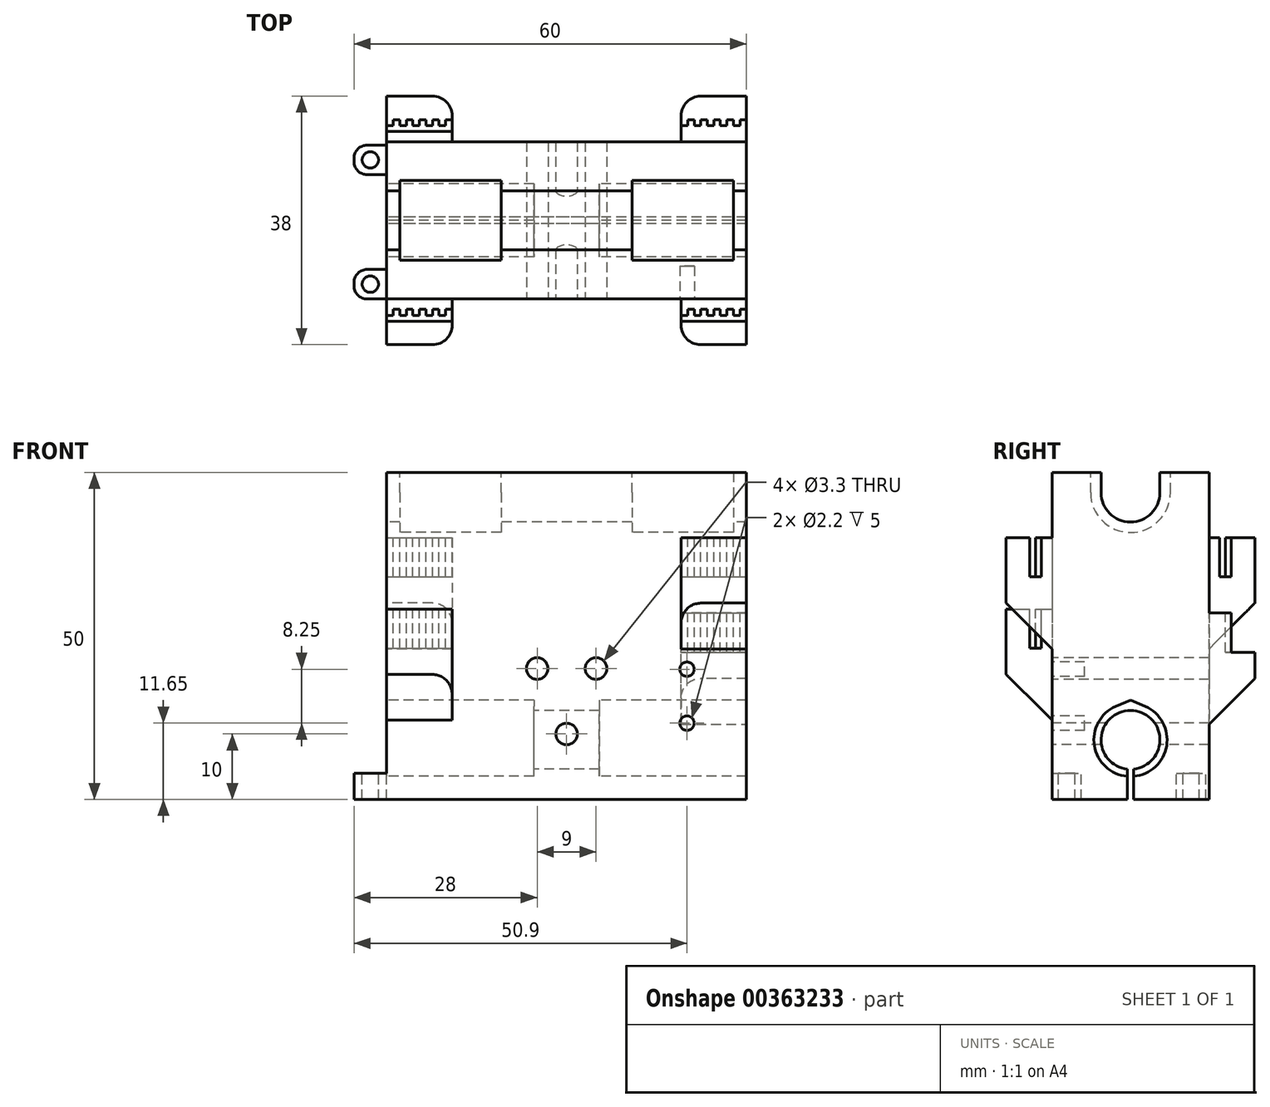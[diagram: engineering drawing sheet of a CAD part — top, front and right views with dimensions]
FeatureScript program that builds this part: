
annotation { "Feature Type Name" : "Feature", "Feature Type Description" : "" }
export const myFeature = defineFeature(function(context is Context, id is Id, definition is map)
    precondition{}
    {
        {
            var Q0;
            Q0=qCreatedBy(makeId("Top.planeOp"),FACE);
            var sketch = newSketch(context, id + "F0", { "sketchPlane" : qUnion([Q0])});
            skLineSegment(sketch, "E0.bottom", {"start": v(0, 0) * mm, "end": v(55, 0) * mm});
            skLineSegment(sketch, "E0.top", {"start": v(0, 24) * mm, "end": v(55, 24) * mm});
            skLineSegment(sketch, "E0.left", {"start": v(0, 0) * mm, "end": v(0, 24) * mm});
            skLineSegment(sketch, "E0.right", {"start": v(55, 0) * mm, "end": v(55, 24) * mm});
            skSolve(sketch);
        }
        {
            var Q0;
            Q0=qSketchRegion(id+"F0",true);
            extrude(context, id + "F1", {"entities" : qUnion([Q0]), "depth" : 50 * mm});
        }
        {
            var Q0;
            Q0=makeQuery(id+"F1.opExtrude","SWEPT_FACE",FACE,{"disambiguationData":[OSD([sQuery(id+"F0.wireOp",EDGE,"E0.left")])]});
            var sketch = newSketch(context, id + "F2", { "sketchPlane" : qUnion([Q0])});
            skCircle(sketch, "E1", {"center": v(-12, 9.1) * mm, "radius": 5.6 * mm});
            skCircle(sketch, "E2", {"center": v(-12, 46.9) * mm, "radius": 4.5 * mm});
            skLineSegment(sketch, "E3", {"start": v(-24, 46.9) * mm, "end": v(0, 46.9) * mm, "construction": true});
            skLineSegment(sketch, "E4", {"start": v(-16.5, 50) * mm, "end": v(-16.5, 46.9) * mm});
            skLineSegment(sketch, "E5", {"start": v(-7.5, 50) * mm, "end": v(-7.5, 46.9) * mm});
            skLineSegment(sketch, "E6", {"start": v(-24, 9.1) * mm, "end": v(0, 9.1) * mm, "construction": true});
            skLineSegment(sketch, "E7", {"start": v(-12, 9.1) * mm, "end": v(-12, 0) * mm, "construction": true});
            skLineSegment(sketch, "E8", {"start": v(-12, 0) * mm, "end": v(-12.5, 0) * mm});
            skLineSegment(sketch, "E9", {"start": v(-12.5, 0) * mm, "end": v(-12.5, 4.63) * mm});
            skLineSegment(sketch, "E10", {"start": v(-12.5, 4.63) * mm, "end": v(-11.5, 4.63) * mm});
            skLineSegment(sketch, "E11", {"start": v(-11.5, 4.63) * mm, "end": v(-11.5, 0) * mm});
            skLineSegment(sketch, "E12", {"start": v(-11.5, 0) * mm, "end": v(-12, 0) * mm});
            skCircle(sketch, "E13", {"center": v(-12, 46.9) * mm, "radius": 6.1 * mm});
            skLineSegment(sketch, "E14", {"start": v(-5.9, 46.9) * mm, "end": v(-5.9, 50) * mm});
            skLineSegment(sketch, "E15", {"start": v(-18.1, 46.9) * mm, "end": v(-18.1, 50) * mm});
            skLineSegment(sketch, "E16", {"start": v(-12, 9.1) * mm, "end": v(-12, 14.7) * mm, "construction": true});
            skLineSegment(sketch, "E17", {"start": v(-12, 14.7) * mm, "end": v(-12, 15.2) * mm, "construction": true});
            skLineSegment(sketch, "E18", {"start": v(-9.73, 14.22) * mm, "end": v(-14.27, 14.22) * mm, "construction": true});
            skLineSegment(sketch, "E19", {"start": v(-12, 15.2) * mm, "end": v(-9.73, 14.22) * mm});
            skLineSegment(sketch, "E20", {"start": v(-12, 15.2) * mm, "end": v(-14.27, 14.22) * mm});
            skCircle(sketch, "E21", {"center": v(-12, 9.1) * mm, "radius": 4.5 * mm});
            skSolve(sketch);
        }
        {
            var Q0;
            {var subQ0=sQuery(id+"F2.wireOp",EDGE,"61a55092-bd36-442a-954f-b1d305e603b2");var subQ1=sQuery(id+"F2.wireOp",EDGE,"E1");var subQ3=makeQuery(id+"F2.imprint","INTERSECT",VERTEX,{"disambiguationData":[OD(0.0)],"derivedFrom":[subQ1,subQ0]});Q0=makeQuery(id+"F2.imprint","IMPRINT",FACE,{"disambiguationData":[TD([[makeQuery(id+"F2.imprint","IMPRINT",EDGE,{"disambiguationData":[TD([[subQ3,-1.0]])],"derivedFrom":subQ1}),1.0]])]});}
            var Q1;
            {var subQ0=sQuery(id+"F2.wireOp",EDGE,"ccdeb851-c584-4ba8-b480-4501c20c5f95");var subQ1=sQuery(id+"F2.wireOp",EDGE,"E1");var subQ3=makeQuery(id+"F2.imprint","INTERSECT",VERTEX,{"disambiguationData":[OD(0.0)],"derivedFrom":[subQ1,subQ0]});Q1=makeQuery(id+"F2.imprint","IMPRINT",FACE,{"disambiguationData":[TD([[makeQuery(id+"F2.imprint","IMPRINT",EDGE,{"disambiguationData":[TD([[subQ3,1.0]])],"derivedFrom":subQ1}),1.0]])]});}
            var Q2;
            Q2=makeQuery(id+"F2.imprint","IMPRINT",FACE,{"disambiguationData":[TD([[makeQuery(id+"F2.imprint","IMPRINT",EDGE,{"derivedFrom":sQuery(id+"F2.wireOp",EDGE,"E8")}),-1.0]])]});
            var Q3;
            {var subQ0=sQuery(id+"F2.wireOp",EDGE,"E10");Q3=makeQuery(id+"F2.imprint","IMPRINT",FACE,{"disambiguationData":[TD([[makeQuery(id+"F2.imprint","IMPRINT",EDGE,{"derivedFrom":subQ0}),-1.0]])]});}
            var Q4;
            {var subQ3=sQuery(id+"F2.wireOp",EDGE,"84843404-b723-4df1-a710-1511c094684b");Q4=makeQuery(id+"F2.imprint","IMPRINT",FACE,{"disambiguationData":[TD([[makeQuery(id+"F2.imprint","IMPRINT",EDGE,{"derivedFrom":subQ3}),-1.0]])]});}
            var Q5;
            {var subQ3=sQuery(id+"F2.wireOp",EDGE,"84843404-b723-4df1-a710-1511c094684b");Q5=makeQuery(id+"F2.imprint","IMPRINT",FACE,{"disambiguationData":[TD([[makeQuery(id+"F2.imprint","IMPRINT",EDGE,{"derivedFrom":subQ3}),1.0]])]});}
            var Q6;
            {var subQ3=sQuery(id+"F2.wireOp",EDGE,"E5");Q6=makeQuery(id+"F2.imprint","IMPRINT",FACE,{"disambiguationData":[TD([[makeQuery(id+"F2.imprint","IMPRINT",EDGE,{"derivedFrom":subQ3}),-1.0]])]});}
            var Q7;
            {var subQ0=sQuery(id+"F2.wireOp",EDGE,"E4");Q7=makeQuery(id+"F2.imprint","IMPRINT",FACE,{"disambiguationData":[TD([[makeQuery(id+"F2.imprint","IMPRINT",EDGE,{"derivedFrom":subQ0}),1.0]])]});}
            var Q8;
            {var subQ0=sQuery(id+"F2.wireOp",EDGE,"E4");Q8=makeQuery(id+"F2.imprint","IMPRINT",FACE,{"disambiguationData":[TD([[makeQuery(id+"F2.imprint","IMPRINT",EDGE,{"derivedFrom":subQ0}),1.0]])]});}
            var Q9;
            {var subQ3=sQuery(id+"F2.wireOp",EDGE,"E5");Q9=makeQuery(id+"F2.imprint","IMPRINT",FACE,{"disambiguationData":[TD([[makeQuery(id+"F2.imprint","IMPRINT",EDGE,{"derivedFrom":subQ3}),-1.0]])]});}
            var Q10;
            {var subQ1=sQuery(id+"F2.wireOp",EDGE,"E2");var subQ4=makeQuery(id+"F2.imprint","INTERSECT",VERTEX,{"derivedFrom":[subQ1,sQuery(id+"F2.wireOp",EDGE,"E5")]});Q10=makeQuery(id+"F2.imprint","IMPRINT",FACE,{"disambiguationData":[TD([[makeQuery(id+"F2.imprint","IMPRINT",EDGE,{"disambiguationData":[TD([[subQ4,-1.0]])],"derivedFrom":subQ1}),1.0]])]});}
            var Q11;
            Q11=makeQuery(id+"F2.imprint","IMPRINT",FACE,{"disambiguationData":[TD([[makeQuery(id+"F2.imprint","IMPRINT",EDGE,{"derivedFrom":sQuery(id+"F2.wireOp",EDGE,"E21")}),1.0]])]});
            var Q12;
            Q12=makeQuery(id+"F1.opExtrude","SWEPT_FACE",FACE,{"disambiguationData":[OSD([sQuery(id+"F0.wireOp",EDGE,"E0.right")])]});
            var Q13;
            {var subQ0=sQuery(id+"F2.wireOp",EDGE,"E9");var subQ1=sQuery(id+"F2.wireOp",EDGE,"E1");var subQ2=makeQuery(id+"F2.imprint","INTERSECT",VERTEX,{"derivedFrom":[subQ1,subQ0]});Q13=makeQuery(id+"F2.imprint","IMPRINT",FACE,{"disambiguationData":[TD([[makeQuery(id+"F2.imprint","IMPRINT",EDGE,{"disambiguationData":[TD([[subQ2,-1.0]])],"derivedFrom":subQ1}),1.0]])]});}
            extrude(context, id + "F3", {"entities" : qUnion([Q0, Q1, Q2, Q3, Q4, Q5, Q6, Q7, Q8, Q9, Q10, Q11, Q12, Q13]), "operationType" : NewBodyOperationType.REMOVE, "endBound" : BoundingType.THROUGH_ALL, "oppositeDirection" : true, "depth" : 25 * mm});
        }
        {
            var Q0;
            {var subQ3=sQuery(id+"F2.wireOp",EDGE,"E4");Q0=makeQuery(id+"F2.imprint","IMPRINT",FACE,{"disambiguationData":[TD([[makeQuery(id+"F2.imprint","IMPRINT",EDGE,{"derivedFrom":subQ3}),-1.0]])]});}
            var Q1;
            {var subQ3=sQuery(id+"F2.wireOp",EDGE,"E15");Q1=makeQuery(id+"F2.imprint","IMPRINT",FACE,{"disambiguationData":[TD([[makeQuery(id+"F2.imprint","IMPRINT",EDGE,{"derivedFrom":subQ3}),-1.0]])]});}
            var Q2;
            {var subQ3=sQuery(id+"F2.wireOp",EDGE,"E14");Q2=makeQuery(id+"F2.imprint","IMPRINT",FACE,{"disambiguationData":[TD([[makeQuery(id+"F2.imprint","IMPRINT",EDGE,{"derivedFrom":subQ3}),1.0]])]});}
            extrude(context, id + "F4", {"entities" : qUnion([Q0, Q1, Q2]), "operationType" : NewBodyOperationType.REMOVE, "oppositeDirection" : true, "depth" : 53 * mm});
        }
        {
            var Q0;
            {var subQ3=sQuery(id+"F2.wireOp",EDGE,"E4");Q0=makeQuery(id+"F2.imprint","IMPRINT",FACE,{"disambiguationData":[TD([[makeQuery(id+"F2.imprint","IMPRINT",EDGE,{"derivedFrom":subQ3}),-1.0]])]});}
            var Q1;
            {var subQ3=sQuery(id+"F2.wireOp",EDGE,"E15");Q1=makeQuery(id+"F2.imprint","IMPRINT",FACE,{"disambiguationData":[TD([[makeQuery(id+"F2.imprint","IMPRINT",EDGE,{"derivedFrom":subQ3}),-1.0]])]});}
            var Q2;
            {var subQ3=sQuery(id+"F2.wireOp",EDGE,"E14");Q2=makeQuery(id+"F2.imprint","IMPRINT",FACE,{"disambiguationData":[TD([[makeQuery(id+"F2.imprint","IMPRINT",EDGE,{"derivedFrom":subQ3}),1.0]])]});}
            extrude(context, id + "F5", {"entities" : qUnion([Q0, Q1, Q2]), "operationType" : NewBodyOperationType.ADD, "oppositeDirection" : true, "depth" : 2 * mm});
        }
        {
            var Q0;
            Q0=makeQuery(id+"F5.opExtrude","CAP_FACE",FACE,{"disambiguationData":[OSD([sQuery(id+"F0.wireOp",EDGE,"E0.left"),sQuery(id+"F2.wireOp",EDGE,"E2"),sQuery(id+"F2.wireOp",EDGE,"E4"),sQuery(id+"F2.wireOp",EDGE,"E5"),sQuery(id+"F2.wireOp",EDGE,"E13"),sQuery(id+"F2.wireOp",EDGE,"E14"),sQuery(id+"F2.wireOp",EDGE,"E15")])],"isStart":false});
            extrude(context, id + "F6", {"entities" : qUnion([Q0]), "operationType" : NewBodyOperationType.ADD, "depth" : 35.5 * mm, "hasSecondDirection" : true, "secondDirectionOppositeDirection" : false, "secondDirectionDepth" : 15.5 * mm});
        }
        {
            var Q0;
            {var subQ0=sQuery(id+"F2.wireOp",EDGE,"E10");Q0=makeQuery(id+"F2.imprint","IMPRINT",FACE,{"disambiguationData":[TD([[makeQuery(id+"F2.imprint","IMPRINT",EDGE,{"derivedFrom":subQ0}),1.0]])]});}
            var Q1;
            {var subQ4=sQuery(id+"F2.wireOp",EDGE,"E1");var subQ8=sQuery(id+"F2.wireOp",EDGE,"E19");var subQ13=makeQuery(id+"F2.imprint","INTERSECT",VERTEX,{"disambiguationData":[OD(1.0)],"derivedFrom":[subQ4,subQ8]});Q1=makeQuery(id+"F2.imprint","IMPRINT",FACE,{"disambiguationData":[TD([[makeQuery(id+"F2.imprint","IMPRINT",EDGE,{"disambiguationData":[TD([[subQ13,-1.0]])],"derivedFrom":subQ4}),1.0]])]});}
            var Q2;
            {var subQ0=sQuery(id+"F2.wireOp",EDGE,"E19");var subQ1=sQuery(id+"F2.wireOp",EDGE,"E1");var subQ2=makeQuery(id+"F2.imprint","INTERSECT",VERTEX,{"disambiguationData":[OD(1.0)],"derivedFrom":[subQ1,subQ0]});Q2=makeQuery(id+"F2.imprint","IMPRINT",FACE,{"disambiguationData":[TD([[makeQuery(id+"F2.imprint","IMPRINT",EDGE,{"disambiguationData":[TD([[subQ2,-1.0]])],"derivedFrom":subQ1}),-1.0]])]});}
            extrude(context, id + "F7", {"entities" : qUnion([Q0, Q1, Q2]), "operationType" : NewBodyOperationType.REMOVE, "oppositeDirection" : true, "depth" : 22.5 * mm});
        }
        {
            var Q0;
            {var subQ0=sQuery(id+"F2.wireOp",EDGE,"E10");Q0=makeQuery(id+"F2.imprint","IMPRINT",FACE,{"disambiguationData":[TD([[makeQuery(id+"F2.imprint","IMPRINT",EDGE,{"derivedFrom":subQ0}),1.0]])]});}
            var Q1;
            {var subQ4=sQuery(id+"F2.wireOp",EDGE,"E1");var subQ8=sQuery(id+"F2.wireOp",EDGE,"E19");var subQ13=makeQuery(id+"F2.imprint","INTERSECT",VERTEX,{"disambiguationData":[OD(1.0)],"derivedFrom":[subQ4,subQ8]});Q1=makeQuery(id+"F2.imprint","IMPRINT",FACE,{"disambiguationData":[TD([[makeQuery(id+"F2.imprint","IMPRINT",EDGE,{"disambiguationData":[TD([[subQ13,-1.0]])],"derivedFrom":subQ4}),1.0]])]});}
            var Q2;
            {var subQ0=sQuery(id+"F2.wireOp",EDGE,"E19");var subQ1=sQuery(id+"F2.wireOp",EDGE,"E1");var subQ2=makeQuery(id+"F2.imprint","INTERSECT",VERTEX,{"disambiguationData":[OD(1.0)],"derivedFrom":[subQ1,subQ0]});Q2=makeQuery(id+"F2.imprint","IMPRINT",FACE,{"disambiguationData":[TD([[makeQuery(id+"F2.imprint","IMPRINT",EDGE,{"disambiguationData":[TD([[subQ2,-1.0]])],"derivedFrom":subQ1}),-1.0]])]});}
            var Q3;
            Q3=makeQuery(id+"F1.opExtrude","SWEPT_FACE",FACE,{"disambiguationData":[OSD([sQuery(id+"F0.wireOp",EDGE,"E0.right")])]});
            extrude(context, id + "F8", {"entities" : qUnion([Q0, Q1, Q2]), "operationType" : NewBodyOperationType.REMOVE, "endBound" : BoundingType.UP_TO_SURFACE, "oppositeDirection" : true, "endBoundEntityFace" : qUnion([Q3]), "depth" : 25 * mm, "hasSecondDirection" : true, "secondDirectionOppositeDirection" : true, "secondDirectionDepth" : 32.5 * mm});
        }
        {
            var Q0;
            Q0=makeQuery(id+"F1.opExtrude","SWEPT_FACE",FACE,{"disambiguationData":[OSD([sQuery(id+"F0.wireOp",EDGE,"E0.bottom")])]});
            var sketch = newSketch(context, id + "F9", { "sketchPlane" : qUnion([Q0])});
            skLineSegment(sketch, "E22.bottom", {"start": v(0, 29.1) * mm, "end": v(10, 29.1) * mm});
            skLineSegment(sketch, "E22.top", {"start": v(0, 9.1) * mm, "end": v(10, 9.1) * mm});
            skLineSegment(sketch, "E22.left", {"start": v(0, 29.1) * mm, "end": v(0, 9.1) * mm});
            skLineSegment(sketch, "E22.right", {"start": v(10, 29.1) * mm, "end": v(10, 9.1) * mm});
            skLineSegment(sketch, "E23.bottom", {"start": v(55, 40) * mm, "end": v(45, 40) * mm});
            skLineSegment(sketch, "E23.top", {"start": v(55, 20) * mm, "end": v(45, 20) * mm});
            skLineSegment(sketch, "E23.left", {"start": v(55, 40) * mm, "end": v(55, 20) * mm});
            skLineSegment(sketch, "E23.right", {"start": v(45, 40) * mm, "end": v(45, 20) * mm});
            skPoint(sketch, "E24", {"position": v(0, 47) * mm});
            skPoint(sketch, "E25", {"position": v(0, 8.6) * mm});
            skSolve(sketch);
        }
        {
            var Q0;
            Q0=qSketchRegion(id+"F9",true);
            extrude(context, id + "F10", {"entities" : qUnion([Q0]), "operationType" : NewBodyOperationType.ADD, "depth" : 7 * mm});
        }
        {
            var Q0;
            Q0=makeQuery(id+"F10.opExtrude","CAP_EDGE",EDGE,{"disambiguationData":[OSD([sQuery(id+"F9.wireOp",EDGE,"E22.top")])],"isStart":false});
            var Q1;
            Q1=makeQuery(id+"F10.opExtrude","CAP_EDGE",EDGE,{"disambiguationData":[OSD([sQuery(id+"F9.wireOp",EDGE,"E23.top")])],"isStart":false});
            chamfer(context, id + "F11", {"entities" : qUnion([Q0, Q1]), "width" : 10 * mm, "tangentPropagation" : true});
        }
        {
            var Q0;
            Q0=makeQuery(id+"F10.opExtrude","SWEPT_FACE",FACE,{"disambiguationData":[OSD([sQuery(id+"F9.wireOp",EDGE,"E22.bottom")])]});
            var sketch = newSketch(context, id + "F12", { "sketchPlane" : qUnion([Q0])});
            skLineSegment(sketch, "E26", {"start": v(-935.9, 0) * mm, "end": v(-935.88, -4.54) * mm});
            skLineSegment(sketch, "E27.left", {"start": v(0, -3.4) * mm, "end": v(0, -1.6) * mm});
            skLineSegment(sketch, "E28", {"start": v(6, -2.5) * mm, "end": v(7, -2.5) * mm});
            skLineSegment(sketch, "E29", {"start": v(4, -2.5) * mm, "end": v(5, -2.5) * mm});
            skLineSegment(sketch, "E30", {"start": v(0, -2.5) * mm, "end": v(1, -2.5) * mm});
            skLineSegment(sketch, "E31", {"start": v(7, -1.6) * mm, "end": v(8, -1.6) * mm});
            skLineSegment(sketch, "E32", {"start": v(2, -2.5) * mm, "end": v(3, -2.5) * mm});
            skLineSegment(sketch, "E33", {"start": v(3, -1.6) * mm, "end": v(4, -1.6) * mm});
            skLineSegment(sketch, "E34", {"start": v(8, -2.5) * mm, "end": v(9, -2.5) * mm});
            skLineSegment(sketch, "E35", {"start": v(8, -1.6) * mm, "end": v(8, -2.5) * mm});
            skLineSegment(sketch, "E36", {"start": v(9, -2.5) * mm, "end": v(9, -1.6) * mm});
            skLineSegment(sketch, "E37", {"start": v(10, -1.6) * mm, "end": v(10, -2.5) * mm});
            skLineSegment(sketch, "E38", {"start": v(6, -1.6) * mm, "end": v(6, -2.5) * mm});
            skLineSegment(sketch, "E39", {"start": v(2, -1.6) * mm, "end": v(2, -2.5) * mm});
            skLineSegment(sketch, "E40", {"start": v(1, -1.6) * mm, "end": v(2, -1.6) * mm});
            skLineSegment(sketch, "E41", {"start": v(1, -2.5) * mm, "end": v(1, -1.6) * mm});
            skLineSegment(sketch, "E42", {"start": v(9, -1.6) * mm, "end": v(10, -1.6) * mm});
            skLineSegment(sketch, "E43", {"start": v(5, -1.6) * mm, "end": v(6, -1.6) * mm});
            skLineSegment(sketch, "E44", {"start": v(5, -2.5) * mm, "end": v(5, -1.6) * mm});
            skLineSegment(sketch, "E45", {"start": v(3, -2.5) * mm, "end": v(3, -1.6) * mm});
            skLineSegment(sketch, "E46", {"start": v(4, -1.6) * mm, "end": v(4, -2.5) * mm});
            skLineSegment(sketch, "E47", {"start": v(7, -2.5) * mm, "end": v(7, -1.6) * mm});
            skLineSegment(sketch, "E48", {"start": v(0, -1.6) * mm, "end": v(0, -2.5) * mm});
            skLineSegment(sketch, "E49", {"start": v(10, -2.5) * mm, "end": v(10, -3.4) * mm});
            skLineSegment(sketch, "E50", {"start": v(0, -3.4) * mm, "end": v(10, -3.4) * mm});
            skLineSegment(sketch, "E51", {"start": v(5.3, -1.6) * mm, "end": v(5.3, 0) * mm});
            skSolve(sketch);
        }
        {
            var Q0;
            Q0=qSketchRegion(id+"F12",true);
            extrude(context, id + "F13", {"entities" : qUnion([Q0]), "operationType" : NewBodyOperationType.REMOVE, "oppositeDirection" : true, "depth" : 6 * mm});
        }
        {
            var Q0;
            Q0=makeQuery(id+"F10.opExtrude","SWEPT_FACE",FACE,{"disambiguationData":[OSD([sQuery(id+"F9.wireOp",EDGE,"E23.bottom")])]});
            var sketch = newSketch(context, id + "F14", { "sketchPlane" : qUnion([Q0])});
            skLineSegment(sketch, "E52.left", {"start": v(45, -3.4) * mm, "end": v(45, -1.6) * mm});
            skLineSegment(sketch, "E53", {"start": v(51, -2.5) * mm, "end": v(52, -2.5) * mm});
            skLineSegment(sketch, "E54", {"start": v(49, -2.5) * mm, "end": v(50, -2.5) * mm});
            skLineSegment(sketch, "E55", {"start": v(45, -2.5) * mm, "end": v(46, -2.5) * mm});
            skLineSegment(sketch, "E56", {"start": v(52, -1.6) * mm, "end": v(53, -1.6) * mm});
            skLineSegment(sketch, "E57", {"start": v(47, -2.5) * mm, "end": v(48, -2.5) * mm});
            skLineSegment(sketch, "E58", {"start": v(48, -1.6) * mm, "end": v(49, -1.6) * mm});
            skLineSegment(sketch, "E59", {"start": v(53, -2.5) * mm, "end": v(54, -2.5) * mm});
            skLineSegment(sketch, "E60", {"start": v(53, -1.6) * mm, "end": v(53, -2.5) * mm});
            skLineSegment(sketch, "E61", {"start": v(54, -2.5) * mm, "end": v(54, -1.6) * mm});
            skLineSegment(sketch, "E62", {"start": v(55, -1.6) * mm, "end": v(55, -2.5) * mm});
            skLineSegment(sketch, "E63", {"start": v(51, -1.6) * mm, "end": v(51, -2.5) * mm});
            skLineSegment(sketch, "E64", {"start": v(47, -1.6) * mm, "end": v(47, -2.5) * mm});
            skLineSegment(sketch, "E65", {"start": v(46, -1.6) * mm, "end": v(47, -1.6) * mm});
            skLineSegment(sketch, "E66", {"start": v(46, -2.5) * mm, "end": v(46, -1.6) * mm});
            skLineSegment(sketch, "E67", {"start": v(54, -1.6) * mm, "end": v(55, -1.6) * mm});
            skLineSegment(sketch, "E68", {"start": v(50, -1.6) * mm, "end": v(51, -1.6) * mm});
            skLineSegment(sketch, "E69", {"start": v(50, -2.5) * mm, "end": v(50, -1.6) * mm});
            skLineSegment(sketch, "E70", {"start": v(48, -2.5) * mm, "end": v(48, -1.6) * mm});
            skLineSegment(sketch, "E71", {"start": v(49, -1.6) * mm, "end": v(49, -2.5) * mm});
            skLineSegment(sketch, "E72", {"start": v(52, -2.5) * mm, "end": v(52, -1.6) * mm});
            skLineSegment(sketch, "E73", {"start": v(45, -1.6) * mm, "end": v(45, -2.5) * mm});
            skLineSegment(sketch, "E74", {"start": v(55, -2.5) * mm, "end": v(55, -3.4) * mm});
            skLineSegment(sketch, "E75", {"start": v(45, -3.4) * mm, "end": v(55, -3.4) * mm});
            skLineSegment(sketch, "E76", {"start": v(50.23, -1.6) * mm, "end": v(50.23, 0) * mm});
            skSolve(sketch);
        }
        {
            var Q0;
            Q0=qSketchRegion(id+"F14",true);
            extrude(context, id + "F15", {"entities" : qUnion([Q0]), "operationType" : NewBodyOperationType.REMOVE, "oppositeDirection" : true, "depth" : 6 * mm});
        }
        {
            var Q0;
            Q0=makeQuery(id+"F1.opExtrude","SWEPT_FACE",FACE,{"disambiguationData":[OSD([sQuery(id+"F0.wireOp",EDGE,"E0.top")])]});
            var sketch = newSketch(context, id + "F16", { "sketchPlane" : qUnion([Q0])});
            skLineSegment(sketch, "E77.bottom", {"start": v(-55, 8.5) * mm, "end": v(-45, 8.5) * mm});
            skLineSegment(sketch, "E77.top", {"start": v(-55, 28.5) * mm, "end": v(-45, 28.5) * mm});
            skLineSegment(sketch, "E77.left", {"start": v(-55, 8.5) * mm, "end": v(-55, 28.5) * mm});
            skLineSegment(sketch, "E77.right", {"start": v(-45, 8.5) * mm, "end": v(-45, 28.5) * mm});
            skLineSegment(sketch, "E78.bottom", {"start": v(0, 40) * mm, "end": v(-10, 40) * mm});
            skLineSegment(sketch, "E78.top", {"start": v(0, 20) * mm, "end": v(-10, 20) * mm});
            skLineSegment(sketch, "E78.left", {"start": v(0, 40) * mm, "end": v(0, 20) * mm});
            skLineSegment(sketch, "E78.right", {"start": v(-10, 40) * mm, "end": v(-10, 20) * mm});
            skSolve(sketch);
        }
        {
            var Q0;
            Q0=qSketchRegion(id+"F16",true);
            extrude(context, id + "F17", {"entities" : qUnion([Q0]), "operationType" : NewBodyOperationType.ADD, "depth" : 7 * mm});
        }
        {
            var Q0;
            Q0=makeQuery(id+"F17.opExtrude","SWEPT_FACE",FACE,{"disambiguationData":[OSD([sQuery(id+"F16.wireOp",EDGE,"E77.top")])]});
            var sketch = newSketch(context, id + "F18", { "sketchPlane" : qUnion([Q0])});
            skLineSegment(sketch, "E79.left", {"start": v(45, 25.6) * mm, "end": v(45, 27.4) * mm});
            skLineSegment(sketch, "E80", {"start": v(51, 26.5) * mm, "end": v(52, 26.5) * mm});
            skLineSegment(sketch, "E81", {"start": v(49, 26.5) * mm, "end": v(50, 26.5) * mm});
            skLineSegment(sketch, "E82", {"start": v(45, 26.5) * mm, "end": v(46, 26.5) * mm});
            skLineSegment(sketch, "E83", {"start": v(52, 27.4) * mm, "end": v(53, 27.4) * mm});
            skLineSegment(sketch, "E84", {"start": v(47, 26.5) * mm, "end": v(48, 26.5) * mm});
            skLineSegment(sketch, "E85", {"start": v(48, 27.4) * mm, "end": v(49, 27.4) * mm});
            skLineSegment(sketch, "E86", {"start": v(53, 26.5) * mm, "end": v(54, 26.5) * mm});
            skLineSegment(sketch, "E87", {"start": v(53, 27.4) * mm, "end": v(53, 26.5) * mm});
            skLineSegment(sketch, "E88", {"start": v(54, 26.5) * mm, "end": v(54, 27.4) * mm});
            skLineSegment(sketch, "E89", {"start": v(55, 27.4) * mm, "end": v(55, 26.5) * mm});
            skLineSegment(sketch, "E90", {"start": v(51, 27.4) * mm, "end": v(51, 26.5) * mm});
            skLineSegment(sketch, "E91", {"start": v(47, 27.4) * mm, "end": v(47, 26.5) * mm});
            skLineSegment(sketch, "E92", {"start": v(46, 27.4) * mm, "end": v(47, 27.4) * mm});
            skLineSegment(sketch, "E93", {"start": v(46, 26.5) * mm, "end": v(46, 27.4) * mm});
            skLineSegment(sketch, "E94", {"start": v(54, 27.4) * mm, "end": v(55, 27.4) * mm});
            skLineSegment(sketch, "E95", {"start": v(50, 27.4) * mm, "end": v(51, 27.4) * mm});
            skLineSegment(sketch, "E96", {"start": v(50, 26.5) * mm, "end": v(50, 27.4) * mm});
            skLineSegment(sketch, "E97", {"start": v(48, 26.5) * mm, "end": v(48, 27.4) * mm});
            skLineSegment(sketch, "E98", {"start": v(49, 27.4) * mm, "end": v(49, 26.5) * mm});
            skLineSegment(sketch, "E99", {"start": v(52, 26.5) * mm, "end": v(52, 27.4) * mm});
            skLineSegment(sketch, "E100", {"start": v(45, 27.4) * mm, "end": v(45, 26.5) * mm});
            skLineSegment(sketch, "E101", {"start": v(55, 26.5) * mm, "end": v(55, 25.6) * mm});
            skLineSegment(sketch, "E102", {"start": v(45, 25.6) * mm, "end": v(55, 25.6) * mm});
            skLineSegment(sketch, "E103", {"start": v(50, 25.6) * mm, "end": v(50, 24) * mm});
            skSolve(sketch);
        }
        {
            var Q0;
            {var subQ4=sQuery(id+"F18.wireOp",EDGE,"E79.left");Q0=makeQuery(id+"F18.imprint","IMPRINT",FACE,{"disambiguationData":[TD([[makeQuery(id+"F18.imprint","IMPRINT",EDGE,{"derivedFrom":subQ4}),1.0]])]});}
            extrude(context, id + "F19", {"entities" : qUnion([Q0]), "operationType" : NewBodyOperationType.REMOVE, "oppositeDirection" : true, "depth" : 6 * mm});
        }
        {
            var Q0;
            Q0=makeQuery(id+"F17.opExtrude","SWEPT_FACE",FACE,{"disambiguationData":[OSD([sQuery(id+"F16.wireOp",EDGE,"E78.bottom")])]});
            var sketch = newSketch(context, id + "F20", { "sketchPlane" : qUnion([Q0])});
            skLineSegment(sketch, "E104", {"start": v(6, 26.5) * mm, "end": v(7, 26.5) * mm});
            skLineSegment(sketch, "E105", {"start": v(4, 26.5) * mm, "end": v(5, 26.5) * mm});
            skLineSegment(sketch, "E106", {"start": v(0, 26.5) * mm, "end": v(1, 26.5) * mm});
            skLineSegment(sketch, "E107", {"start": v(7, 27.4) * mm, "end": v(8, 27.4) * mm});
            skLineSegment(sketch, "E108", {"start": v(2, 26.5) * mm, "end": v(3, 26.5) * mm});
            skLineSegment(sketch, "E109", {"start": v(3, 27.4) * mm, "end": v(4, 27.4) * mm});
            skLineSegment(sketch, "E110", {"start": v(8, 26.5) * mm, "end": v(9, 26.5) * mm});
            skLineSegment(sketch, "E111", {"start": v(8, 27.4) * mm, "end": v(8, 26.5) * mm});
            skLineSegment(sketch, "E112", {"start": v(9, 26.5) * mm, "end": v(9, 27.4) * mm});
            skLineSegment(sketch, "E113", {"start": v(10, 27.4) * mm, "end": v(10, 26.5) * mm});
            skLineSegment(sketch, "E114", {"start": v(6, 27.4) * mm, "end": v(6, 26.5) * mm});
            skLineSegment(sketch, "E115", {"start": v(2, 27.4) * mm, "end": v(2, 26.5) * mm});
            skLineSegment(sketch, "E116", {"start": v(1, 27.4) * mm, "end": v(2, 27.4) * mm});
            skLineSegment(sketch, "E117", {"start": v(1, 26.5) * mm, "end": v(1, 27.4) * mm});
            skLineSegment(sketch, "E118", {"start": v(9, 27.4) * mm, "end": v(10, 27.4) * mm});
            skLineSegment(sketch, "E119", {"start": v(5, 27.4) * mm, "end": v(6, 27.4) * mm});
            skLineSegment(sketch, "E120", {"start": v(5, 26.5) * mm, "end": v(5, 27.4) * mm});
            skLineSegment(sketch, "E121", {"start": v(3, 26.5) * mm, "end": v(3, 27.4) * mm});
            skLineSegment(sketch, "E122", {"start": v(4, 27.4) * mm, "end": v(4, 26.5) * mm});
            skLineSegment(sketch, "E123", {"start": v(7, 26.5) * mm, "end": v(7, 27.4) * mm});
            skLineSegment(sketch, "E124", {"start": v(10, 26.5) * mm, "end": v(10, 25.6) * mm});
            skLineSegment(sketch, "E125", {"start": v(0, 25.6) * mm, "end": v(10, 25.6) * mm});
            skLineSegment(sketch, "E126", {"start": v(5, 25.6) * mm, "end": v(5, 24) * mm});
            skLineSegment(sketch, "E127", {"start": v(0, 25.6) * mm, "end": v(0, 26.5) * mm});
            skSolve(sketch);
        }
        {
            var Q0;
            Q0=makeQuery(id+"F20.imprint","IMPRINT",FACE,{"disambiguationData":[TD([[makeQuery(id+"F20.imprint","IMPRINT",EDGE,{"derivedFrom":sQuery(id+"F20.wireOp",EDGE,"E104")}),-1.0]])]});
            extrude(context, id + "F21", {"entities" : qUnion([Q0]), "operationType" : NewBodyOperationType.REMOVE, "oppositeDirection" : true, "depth" : 6 * mm});
        }
        {
            var Q0;
            Q0=makeQuery(id+"F17.opExtrude","CAP_EDGE",EDGE,{"disambiguationData":[OSD([sQuery(id+"F16.wireOp",EDGE,"E78.top")])],"isStart":false});
            var Q1;
            Q1=makeQuery(id+"F17.opExtrude","CAP_EDGE",EDGE,{"disambiguationData":[OSD([sQuery(id+"F16.wireOp",EDGE,"E77.bottom")])],"isStart":false});
            chamfer(context, id + "F22", {"entities" : qUnion([Q0, Q1]), "width" : 10 * mm, "tangentPropagation" : true});
        }
        {
            var Q0;
            Q0=makeQuery(id+"F1.opExtrude","SWEPT_FACE",FACE,{"disambiguationData":[OSD([sQuery(id+"F0.wireOp",EDGE,"E0.bottom")])]});
            var sketch = newSketch(context, id + "F23", { "sketchPlane" : qUnion([Q0])});
            skCircle(sketch, "E128", {"center": v(32, 20) * mm, "radius": 1.65 * mm});
            skCircle(sketch, "E129", {"center": v(27.5, 10) * mm, "radius": 1.65 * mm});
            skLineSegment(sketch, "E130", {"start": v(27.5, 0) * mm, "end": v(27.5, 13.82) * mm, "construction": true});
            skCircle(sketch, "E131", {"center": v(23, 20) * mm, "radius": 1.65 * mm});
            skLineSegment(sketch, "E132", {"start": v(23, 20) * mm, "end": v(32, 20) * mm, "construction": true});
            skPoint(sketch, "E133", {"position": v(27.5, 20) * mm});
            skSolve(sketch);
        }
        {
            var Q0;
            Q0=qSketchRegion(id+"F23",true);
            var Q1;
            Q1=makeQuery(id+"F23.imprint","IMPRINT",FACE,{"disambiguationData":[TD([[makeQuery(id+"F23.imprint","IMPRINT",EDGE,{"derivedFrom":sQuery(id+"F23.wireOp",EDGE,"f3b199d0-cdf7-4ae0-8cf6-aff4b2f50aa2")}),1.0]])]});
            var Q2;
            Q2=makeQuery(id+"F23.imprint","IMPRINT",FACE,{"disambiguationData":[TD([[makeQuery(id+"F23.imprint","IMPRINT",EDGE,{"derivedFrom":sQuery(id+"F23.wireOp",EDGE,"ba15866d-b390-47b8-8f7e-ce56b43dcf09")}),1.0]])]});
            var Q3;
            Q3=makeQuery(id+"F23.imprint","IMPRINT",FACE,{"disambiguationData":[TD([[makeQuery(id+"F23.imprint","IMPRINT",EDGE,{"derivedFrom":sQuery(id+"F23.wireOp",EDGE,"E128")}),1.0]])]});
            var Q4;
            Q4=makeQuery(id+"F23.imprint","IMPRINT",FACE,{"disambiguationData":[TD([[makeQuery(id+"F23.imprint","IMPRINT",EDGE,{"derivedFrom":sQuery(id+"F23.wireOp",EDGE,"35e56f97-7b7a-4fd1-a2f6-4374f54c4edf")}),1.0]])]});
            extrude(context, id + "F24", {"entities" : qUnion([Q0, Q1, Q2, Q3, Q4]), "operationType" : NewBodyOperationType.REMOVE, "endBound" : BoundingType.THROUGH_ALL, "oppositeDirection" : true, "depth" : 25 * mm});
        }
        {
            var Q0;
            Q0=makeQuery(id+"F1.opExtrude","SWEPT_FACE",FACE,{"disambiguationData":[OSD([sQuery(id+"F0.wireOp",EDGE,"E0.bottom")])]});
            var sketch = newSketch(context, id + "F25", { "sketchPlane" : qUnion([Q0])});
            skCircle(sketch, "E134", {"center": v(45.9, 19.9) * mm, "radius": 1.1 * mm});
            skCircle(sketch, "E135", {"center": v(45.9, 11.65) * mm, "radius": 1.1 * mm});
            skSolve(sketch);
        }
        {
            var Q0;
            Q0=qSketchRegion(id+"F25",true);
            extrude(context, id + "F26", {"entities" : qUnion([Q0]), "operationType" : NewBodyOperationType.REMOVE, "oppositeDirection" : true, "depth" : 5 * mm});
        }
        {
            var Q0;
            {var subQ0=sQuery(id+"F0.wireOp",EDGE,"E0.left");Q0=makeQuery(id+"F17.boolean.opBoolean","MERGE",FACE,{"derivedFrom":[makeQuery(id+"F10.boolean.opBoolean","MERGE",FACE,{"derivedFrom":[makeQuery(id+"F5.boolean.opBoolean","MERGE",FACE,{"derivedFrom":[makeQuery(id+"F1.opExtrude","SWEPT_FACE",FACE,{"disambiguationData":[OSD([subQ0])]}),makeQuery(id+"F5.opExtrude","CAP_FACE",FACE,{"disambiguationData":[OSD([subQ0,sQuery(id+"F2.wireOp",EDGE,"E2"),sQuery(id+"F2.wireOp",EDGE,"E4"),sQuery(id+"F2.wireOp",EDGE,"E5"),sQuery(id+"F2.wireOp",EDGE,"E13"),sQuery(id+"F2.wireOp",EDGE,"E14"),sQuery(id+"F2.wireOp",EDGE,"E15")])],"isStart":true})]}),makeQuery(id+"F10.opExtrude","SWEPT_FACE",FACE,{"disambiguationData":[OSD([sQuery(id+"F9.wireOp",EDGE,"E22.left")])]})]}),makeQuery(id+"F17.opExtrude","SWEPT_FACE",FACE,{"disambiguationData":[OSD([sQuery(id+"F16.wireOp",EDGE,"E78.left")])]})]});}
            var sketch = newSketch(context, id + "F27", { "sketchPlane" : qUnion([Q0])});
            skLineSegment(sketch, "E136.bottom", {"start": v(0, 0) * mm, "end": v(-4.5, 0) * mm});
            skLineSegment(sketch, "E136.top", {"start": v(0, 4) * mm, "end": v(-4.5, 4) * mm});
            skLineSegment(sketch, "E136.left", {"start": v(0, 0) * mm, "end": v(0, 4) * mm});
            skLineSegment(sketch, "E136.right", {"start": v(-4.5, 0) * mm, "end": v(-4.5, 4) * mm});
            skLineSegment(sketch, "E137.bottom", {"start": v(-19, 0) * mm, "end": v(-23.5, 0) * mm});
            skLineSegment(sketch, "E137.top", {"start": v(-19, 4) * mm, "end": v(-23.5, 4) * mm});
            skLineSegment(sketch, "E137.left", {"start": v(-19, 0) * mm, "end": v(-19, 4) * mm});
            skLineSegment(sketch, "E137.right", {"start": v(-23.5, 0) * mm, "end": v(-23.5, 4) * mm});
            skSolve(sketch);
        }
        {
            var Q0;
            Q0=qSketchRegion(id+"F27",true);
            extrude(context, id + "F28", {"entities" : qUnion([Q0]), "operationType" : NewBodyOperationType.ADD, "depth" : 5 * mm});
        }
        {
            var Q0;
            Q0=makeQuery(id+"F28.opExtrude","SWEPT_FACE",FACE,{"disambiguationData":[OSD([sQuery(id+"F27.wireOp",EDGE,"E136.top")])]});
            var sketch = newSketch(context, id + "F29", { "sketchPlane" : qUnion([Q0])});
            skLineSegment(sketch, "E138", {"start": v(-2.5, 4.5) * mm, "end": v(-2.5, 0) * mm, "construction": true});
            skCircle(sketch, "E139", {"center": v(-2.5, 2.25) * mm, "radius": 1.25 * mm});
            skLineSegment(sketch, "E140", {"start": v(-2.5, 4.5) * mm, "end": v(-2.5, 23.79) * mm, "construction": true});
            skCircle(sketch, "E141", {"center": v(-2.5, 21.25) * mm, "radius": 1.25 * mm});
            skSolve(sketch);
        }
        {
            var Q0;
            Q0=qSketchRegion(id+"F29",true);
            extrude(context, id + "F30", {"entities" : qUnion([Q0]), "operationType" : NewBodyOperationType.REMOVE, "oppositeDirection" : true, "depth" : 25 * mm});
        }
        {
            var Q0;
            Q0=makeQuery(id+"F28.opExtrude","CAP_EDGE",EDGE,{"disambiguationData":[OSD([sQuery(id+"F27.wireOp",EDGE,"E136.right")])],"isStart":false});
            var Q1;
            Q1=makeQuery(id+"F28.opExtrude","CAP_EDGE",EDGE,{"disambiguationData":[OSD([sQuery(id+"F27.wireOp",EDGE,"E136.left")])],"isStart":false});
            var Q2;
            Q2=makeQuery(id+"F28.opExtrude","CAP_EDGE",EDGE,{"disambiguationData":[OSD([sQuery(id+"F27.wireOp",EDGE,"E137.left")])],"isStart":false});
            var Q3;
            Q3=makeQuery(id+"F28.opExtrude","CAP_EDGE",EDGE,{"disambiguationData":[OSD([sQuery(id+"F27.wireOp",EDGE,"E137.right")])],"isStart":false});
            fillet(context, id + "F31", {"entities" : qUnion([Q0, Q1, Q2, Q3]), "radius" : 2 * mm, "tangentPropagation" : true, "allowEdgeOverflow" : false});
        }
        {
            var Q0;
            Q0=makeQuery(id+"F10.opExtrude","CAP_EDGE",EDGE,{"disambiguationData":[OSD([sQuery(id+"F9.wireOp",EDGE,"E22.right")])],"isStart":false});
            var Q1;
            Q1=makeQuery(id+"F10.opExtrude","CAP_EDGE",EDGE,{"disambiguationData":[OSD([sQuery(id+"F9.wireOp",EDGE,"E23.right")])],"isStart":false});
            var Q2;
            Q2=makeQuery(id+"F17.opExtrude","CAP_EDGE",EDGE,{"disambiguationData":[OSD([sQuery(id+"F16.wireOp",EDGE,"E78.right")])],"isStart":false});
            var Q3;
            Q3=makeQuery(id+"F17.opExtrude","CAP_EDGE",EDGE,{"disambiguationData":[OSD([sQuery(id+"F16.wireOp",EDGE,"E77.right")])],"isStart":false});
            fillet(context, id + "F32", {"entities" : qUnion([Q0, Q1, Q2, Q3]), "radius" : 3 * mm, "tangentPropagation" : true, "allowEdgeOverflow" : false});
        }
    });
